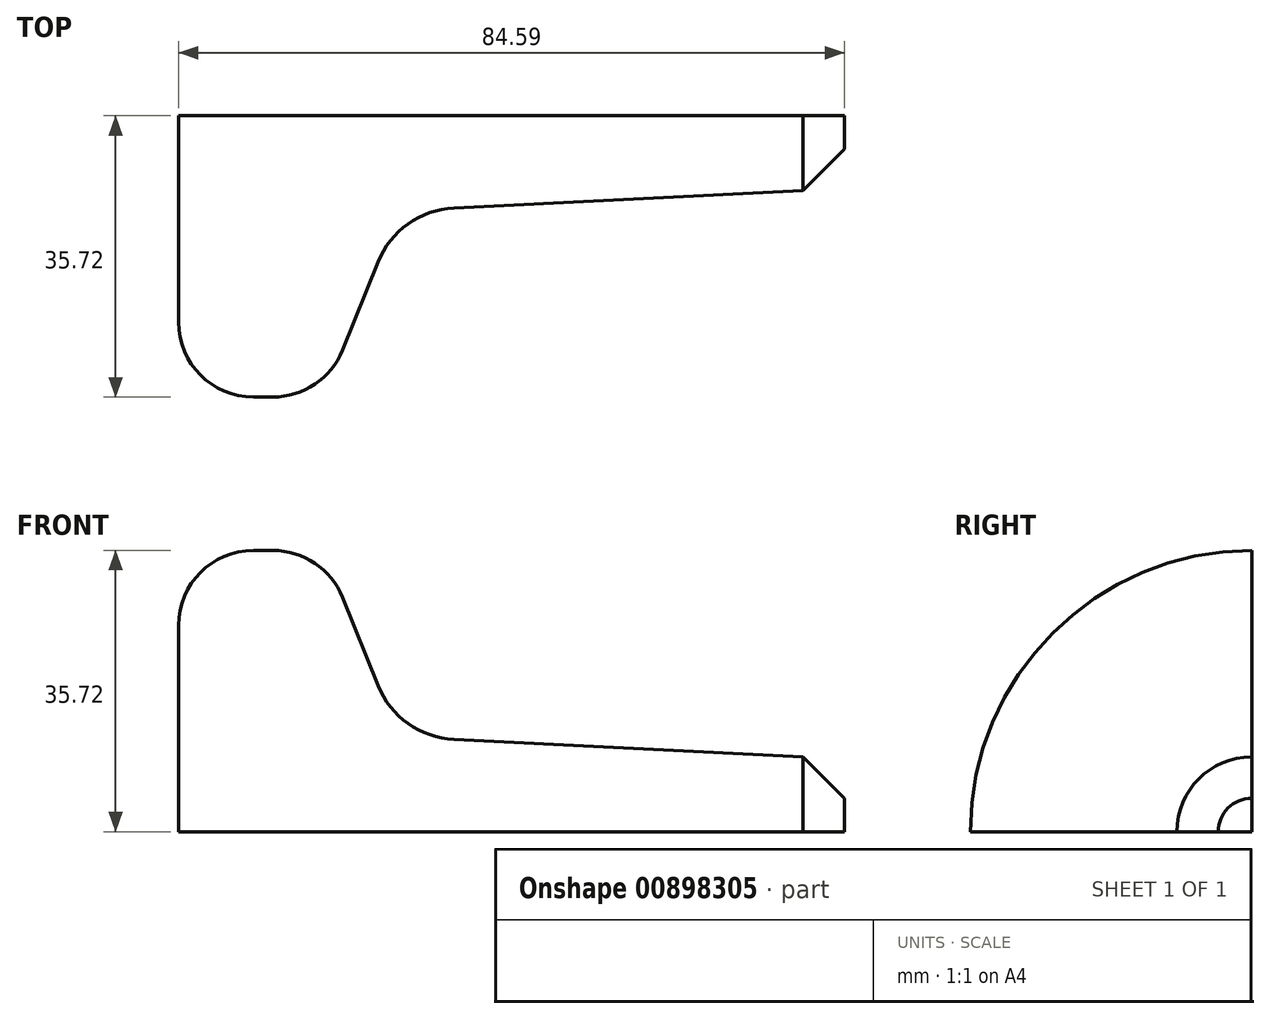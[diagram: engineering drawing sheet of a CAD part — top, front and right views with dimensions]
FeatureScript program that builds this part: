
annotation { "Feature Type Name" : "Feature", "Feature Type Description" : "" }
export const myFeature = defineFeature(function(context is Context, id is Id, definition is map)
    precondition{}
    {
        {
            var Q0;
            Q0=qCreatedBy(makeId("Front.planeOp"),FACE);
            var sketch = newSketch(context, id + "F0", { "sketchPlane" : qUnion([Q0])});
            skLineSegment(sketch, "E0", {"start": v(0, 0) * mm, "end": v(78.13, 0) * mm, "construction": true});
            skLineSegment(sketch, "E1", {"start": v(0, 23.65) * mm, "end": v(-4.89, 23.65) * mm, "construction": true});
            skLineSegment(sketch, "E2", {"start": v(-9.5, 0) * mm, "end": v(-9.5, 14.15) * mm});
            skPoint(sketch, "E3", {"position": v(0, 14.15) * mm});
            skArc(sketch, "E4", {"start": v(0, 23.65) * mm, "mid": v(-6.72, 20.87) * mm, "end": v(-9.5, 14.15) * mm});
            skLineSegment(sketch, "E5", {"start": v(0, 23.65) * mm, "end": v(2.5, 23.65) * mm});
            skPoint(sketch, "E6", {"position": v(2.5, 14.15) * mm});
            skPoint(sketch, "E7", {"position": v(12, 14.15) * mm});
            skArc(sketch, "E8", {"start": v(12, 14.15) * mm, "mid": v(9.22, 20.87) * mm, "end": v(2.5, 23.65) * mm});
            skLineSegment(sketch, "E9", {"start": v(11.3, 17.7) * mm, "end": v(15.83, 6.51) * mm});
            skLineSegment(sketch, "E10", {"start": v(25.48, -0.35) * mm, "end": v(75.09, -2.83) * mm});
            skLineSegment(sketch, "E11.right", {"start": v(75.09, -2.83) * mm, "end": v(75.09, -12.07) * mm});
            skLineSegment(sketch, "E12", {"start": v(-9.5, 0) * mm, "end": v(-9.5, -12.07) * mm});
            skLineSegment(sketch, "E13", {"start": v(75.09, -12.07) * mm, "end": v(-9.5, -12.07) * mm});
            skLineSegment(sketch, "E14", {"start": v(75.09, -7.83) * mm, "end": v(77.82, -7.83) * mm, "construction": true});
            skLineSegment(sketch, "E15", {"start": v(75.09, -7.83) * mm, "end": v(69.83, -2.57) * mm});
            skPoint(sketch, "E16.visualSharp", {"position": v(18.46, 0) * mm});
            skArc(sketch, "E16.filletArc", {"start": v(15.83, 6.51) * mm, "mid": v(19.65, 1.67) * mm, "end": v(25.48, -0.35) * mm});
            skSolve(sketch);
        }
        {
            var Q0;
            Q0=makeQuery(id+"F0.imprint","IMPRINT",FACE,{"disambiguationData":[TD([[makeQuery(id+"F0.imprint","IMPRINT",EDGE,{"derivedFrom":sQuery(id+"F0.wireOp",EDGE,"E2")}),-1.0]])]});
            var Q1;
            Q1=sQuery(id+"F0.wireOp",EDGE,"E13");
            revolve(context, id + "F1", {"surfaceOperationType" : NewSurfaceOperationType.NEW, "entities" : qUnion([Q0]), "axis" : qUnion([Q1]), "revolveType" : RevolveType.FULL});
        }
        {
            var Q0;
            Q0=makeQuery(id+"F1.opRevolve","SWEPT_FACE",FACE,{"disambiguationData":[OSD([sQuery(id+"F0.wireOp",EDGE,"E2"),sQuery(id+"F0.wireOp",EDGE,"E12")])]});
            var sketch = newSketch(context, id + "F2", { "sketchPlane" : qUnion([Q0])});
            skCircle(sketch, "E17.0", {"center": v(0, -12.07) * mm, "radius": 26.22 * mm});
            skLineSegment(sketch, "E18", {"start": v(0, -12.07) * mm, "end": v(0, 25.85) * mm});
            skLineSegment(sketch, "E19", {"start": v(0, -12.07) * mm, "end": v(43.14, -12.07) * mm});
            skLineSegment(sketch, "E20", {"start": v(0, 25.85) * mm, "end": v(-45.26, 25.85) * mm});
            skLineSegment(sketch, "E21", {"start": v(-45.26, 25.85) * mm, "end": v(-45.26, -49.24) * mm});
            skLineSegment(sketch, "E22", {"start": v(-45.26, -49.24) * mm, "end": v(43.14, -49.24) * mm});
            skLineSegment(sketch, "E23", {"start": v(43.14, -12.07) * mm, "end": v(43.14, -49.24) * mm});
            skSolve(sketch);
        }
        {
            var Q0;
            {var subQ4=sQuery(id+"F2.wireOp",EDGE,"E20");Q0=makeQuery(id+"F2.imprint","IMPRINT",FACE,{"disambiguationData":[TD([[makeQuery(id+"F2.imprint","IMPRINT",EDGE,{"derivedFrom":subQ4}),1.0]])]});}
            var Q1;
            {var subQ0=sQuery(id+"F2.wireOp",EDGE,"E18");var subQ1=sQuery(id+"F2.wireOp",EDGE,"E17.0");var subQ2=makeQuery(id+"F2.imprint","INTERSECT",VERTEX,{"derivedFrom":[subQ1,subQ0]});Q1=makeQuery(id+"F2.imprint","IMPRINT",FACE,{"disambiguationData":[TD([[makeQuery(id+"F2.imprint","IMPRINT",EDGE,{"disambiguationData":[TD([[subQ2,1.0]])],"derivedFrom":subQ1}),-1.0]])]});}
            extrude(context, id + "F3", {"entities" : qUnion([Q0, Q1]), "operationType" : NewBodyOperationType.REMOVE, "oppositeDirection" : true, "depth" : 100 * mm, "offsetDistance" : 25 * mm});
        }
    });
